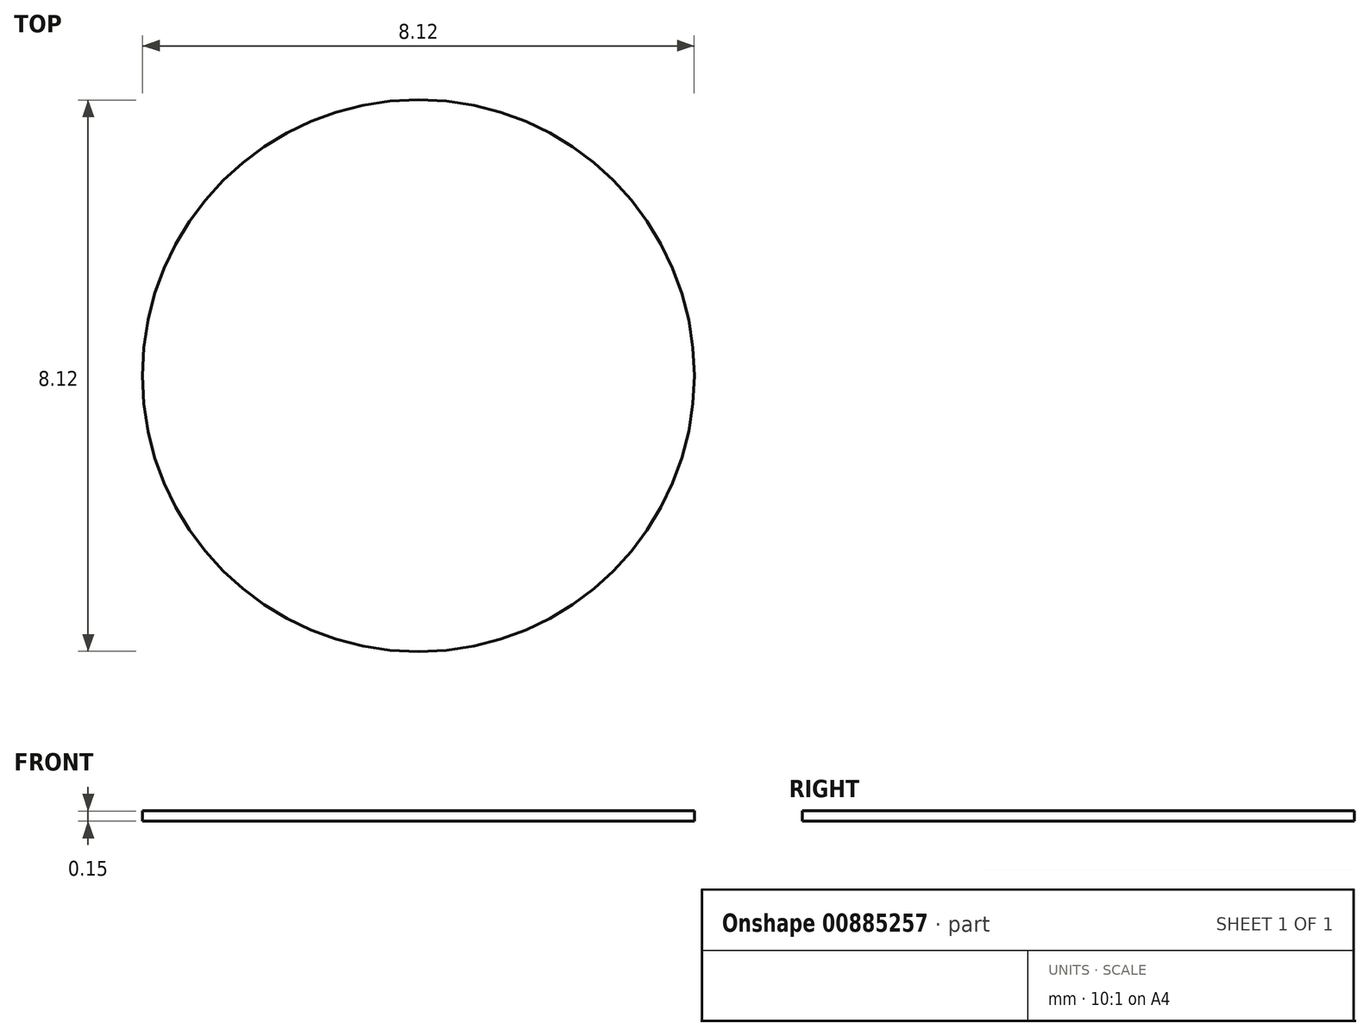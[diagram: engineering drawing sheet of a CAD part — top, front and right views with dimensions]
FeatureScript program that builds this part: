
annotation { "Feature Type Name" : "Feature", "Feature Type Description" : "" }
export const myFeature = defineFeature(function(context is Context, id is Id, definition is map)
    precondition{}
    {
        {
            var Q0;
            Q0=qCreatedBy(makeId("Top.planeOp"),FACE);
            var sketch = newSketch(context, id + "F0", { "sketchPlane" : qUnion([Q0])});
            skCircle(sketch, "E0", {"center": v(0, 0) * mm, "radius": 4.06 * mm});
            skSolve(sketch);
        }
        {
            var Q0;
            Q0=makeQuery(id+"F0.imprint","IMPRINT",FACE,{"disambiguationData":[TD([[makeQuery(id+"F0.imprint","IMPRINT",EDGE,{"derivedFrom":sQuery(id+"F0.wireOp",EDGE,"E0")}),1.0]])]});
            extrude(context, id + "F1", {"entities" : qUnion([Q0]), "depth" : 0.15 * mm, "offsetDistance" : 25 * mm});
        }
    });
